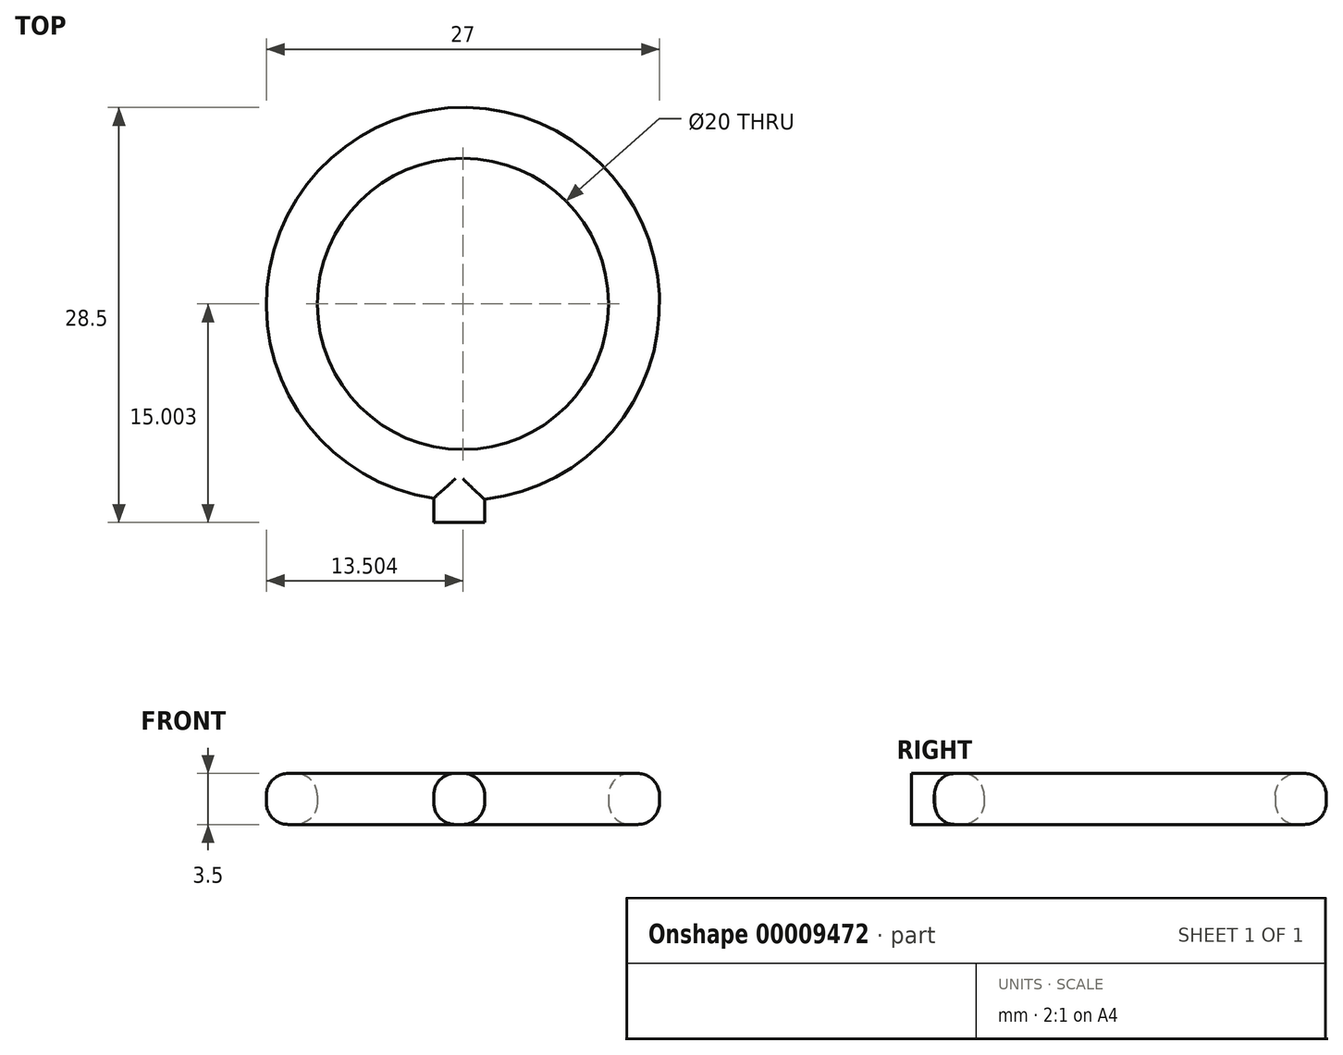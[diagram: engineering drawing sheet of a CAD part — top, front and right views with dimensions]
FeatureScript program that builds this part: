
annotation { "Feature Type Name" : "Feature", "Feature Type Description" : "" }
export const myFeature = defineFeature(function(context is Context, id is Id, definition is map)
    precondition{}
    {
        {
            var Q0;
            Q0=qCreatedBy(makeId("Top.planeOp"),FACE);
            var sketch = newSketch(context, id + "F0", { "sketchPlane" : qUnion([Q0])});
            skLineSegment(sketch, "E0.top", {"start": v(-39.25, -37.84) * mm, "end": v(-35.75, -37.84) * mm});
            skLineSegment(sketch, "E0.left", {"start": v(-39.25, -36.19) * mm, "end": v(-39.25, -37.84) * mm});
            skLineSegment(sketch, "E0.right", {"start": v(-35.75, -36.26) * mm, "end": v(-35.75, -37.84) * mm});
            skArc(sketch, "E1", {"start": v(-35.75, -36.26) * mm, "mid": v(-36.97, -9.34) * mm, "end": v(-39.25, -36.19) * mm});
            skCircle(sketch, "E2", {"center": v(-37.24, -22.84) * mm, "radius": 10 * mm});
            skSolve(sketch);
        }
        {
            var Q0;
            Q0 = qSketchRegion(id + "F0", true);
            extrude(context, id + "F1", {"entities" : qUnion([Q0]), "depth" : 3.5 * mm});
        }
        {
            var Q0;
            Q0=makeQuery(id+"F1.opExtrude","CAP_EDGE",EDGE,{"disambiguationData":[OSD([sQuery(id+"F0.wireOp",EDGE,"E1")])],"isStart":false});
            var Q1;
            Q1=makeQuery(id+"F1.opExtrude","CAP_EDGE",EDGE,{"disambiguationData":[OSD([sQuery(id+"F0.wireOp",EDGE,"E2")])],"isStart":false});
            var Q2;
            Q2=makeQuery(id+"F1.opExtrude","CAP_EDGE",EDGE,{"disambiguationData":[OSD([sQuery(id+"F0.wireOp",EDGE,"E0.right")])],"isStart":false});
            var Q3;
            Q3=makeQuery(id+"F1.opExtrude","CAP_EDGE",EDGE,{"disambiguationData":[OSD([sQuery(id+"F0.wireOp",EDGE,"E0.left")])],"isStart":false});
            var Q4;
            Q4=makeQuery(id+"F1.opExtrude","CAP_EDGE",EDGE,{"disambiguationData":[OSD([sQuery(id+"F0.wireOp",EDGE,"E1")])],"isStart":true});
            var Q5;
            Q5=makeQuery(id+"F1.opExtrude","CAP_EDGE",EDGE,{"disambiguationData":[OSD([sQuery(id+"F0.wireOp",EDGE,"E0.right")])],"isStart":true});
            var Q6;
            Q6=makeQuery(id+"F1.opExtrude","CAP_EDGE",EDGE,{"disambiguationData":[OSD([sQuery(id+"F0.wireOp",EDGE,"E0.left")])],"isStart":true});
            var Q7;
            Q7=makeQuery(id+"F1.opExtrude","CAP_EDGE",EDGE,{"disambiguationData":[OSD([sQuery(id+"F0.wireOp",EDGE,"E2")])],"isStart":true});
            fillet(context, id + "F2", {"entities" : qUnion([Q0, Q1, Q2, Q3, Q4, Q5, Q6, Q7]), "radius" : 1.5 * mm, "tangentPropagation" : true, "allowEdgeOverflow" : false});
        }
    });
